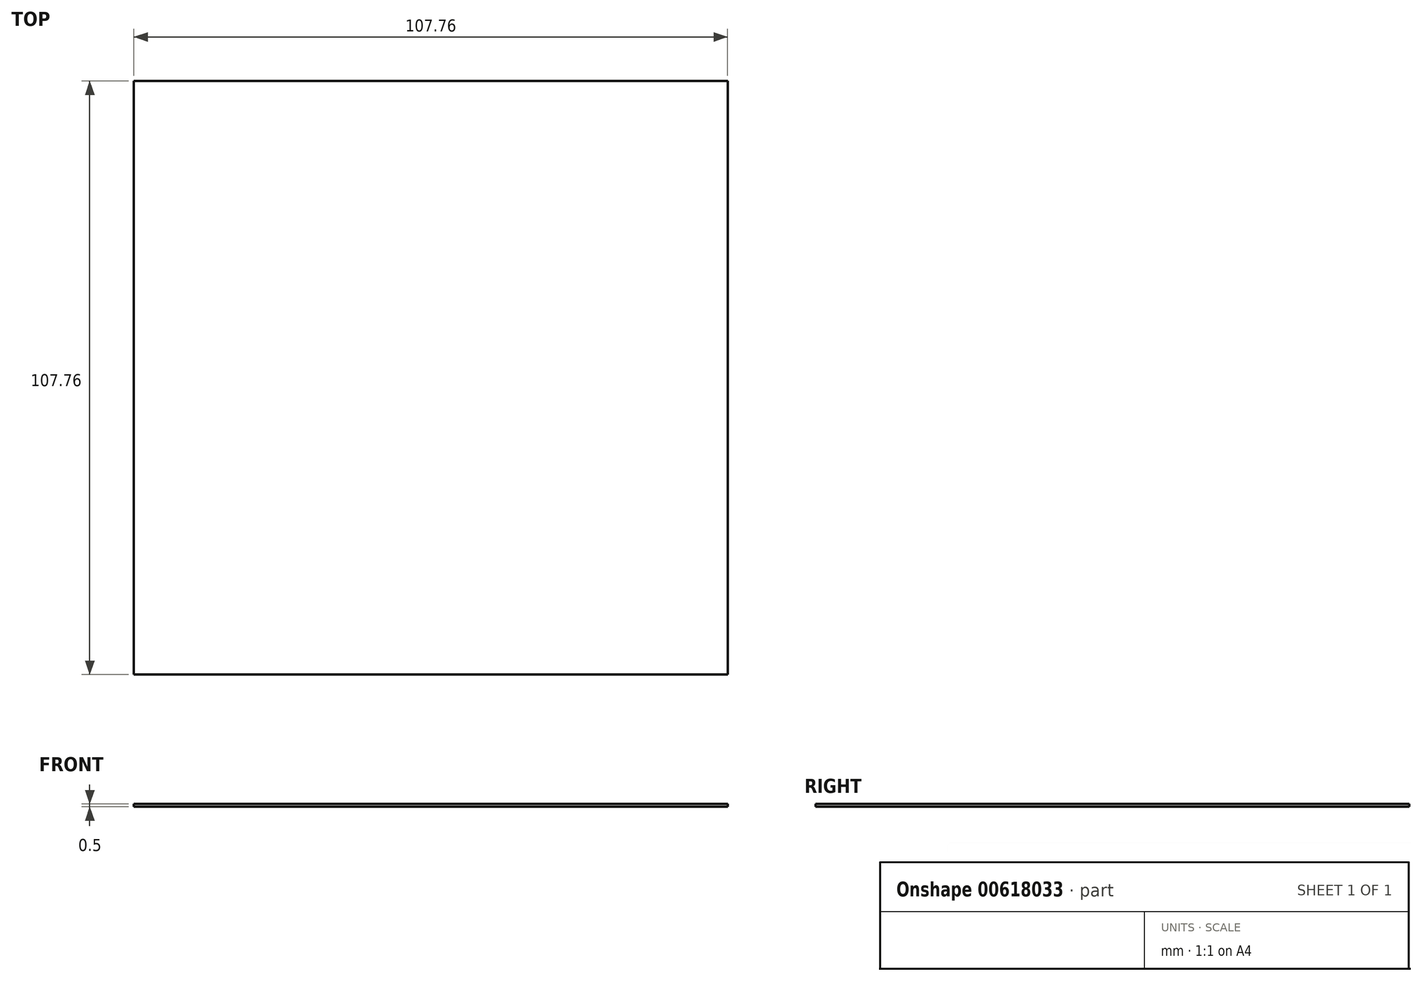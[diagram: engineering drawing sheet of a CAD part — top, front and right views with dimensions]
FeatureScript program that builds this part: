
annotation { "Feature Type Name" : "Feature", "Feature Type Description" : "" }
export const myFeature = defineFeature(function(context is Context, id is Id, definition is map)
    precondition{}
    {
        {
            var Q0;
            Q0=qCreatedBy(makeId("Top.planeOp"),FACE);
            var sketch = newSketch(context, id + "F0", { "sketchPlane" : qUnion([Q0])});
            skLineSegment(sketch, "E0.bottom", {"start": v(53.88, 53.88) * mm, "end": v(-53.88, 53.88) * mm});
            skLineSegment(sketch, "E0.top", {"start": v(53.88, -53.88) * mm, "end": v(-53.88, -53.88) * mm});
            skLineSegment(sketch, "E0.left", {"start": v(53.88, 53.88) * mm, "end": v(53.88, -53.88) * mm});
            skLineSegment(sketch, "E0.right", {"start": v(-53.88, 53.88) * mm, "end": v(-53.88, -53.88) * mm});
            skPoint(sketch, "E0.middle", {"position": v(0, 0) * mm});
            skSolve(sketch);
        }
        {
            var Q0;
            Q0 = qSketchRegion(id + "F0", true);
            extrude(context, id + "F1", {"entities" : qUnion([Q0]), "depth" : .5 * mm, "offsetDistance" : 25.4 * mm});
        }
    });
